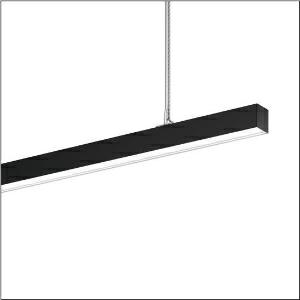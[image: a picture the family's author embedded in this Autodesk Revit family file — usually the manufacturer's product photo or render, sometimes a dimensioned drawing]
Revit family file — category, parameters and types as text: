
# Revit family: silica_r__21_51mx30da44bb_2b52
name_source: partatom
category: Lighting Fixtures
units: mm (PartAtom-declared; Revit-internal decimal feet)

## family parameters
Cut with Voids When Loaded = No
Host = Face
Light Source = No
Part Type = Normal
Room Calculation Point = No
Round Connector Dimension = Use Diameter
Shared = No

## types (1)
- --- (1 x LED, 4210 lm, 26 W, 4000K)
    Apparent Load = 26 VA
    CIE Flux Codes = 47 79 96 57 100
    Color Rendering = 80
    Color Temperature = 4000K
    Default Elevation = 1800 mm
    Description = Silica® 21, office luminaire, primary optical cover: cover, of PMMA, opal, light emission: direct/indirect distribution, primary light characteristic: symmetric, installation type: suspended mounting, LED, rated luminous flux: 4.210lm, luminous efficacy: 162lm/W, light colour: 840, colour temperature: 4000K, with terminal, 3+2-pole, max. 2.5mm², mains connection: 220..240V, AC, 50/60Hz, rated input power: 26W, luminaire housing, of aluminium, jet black (RAL 9005), length: 1.204mm, width: 53mm, height: 53mm, protection rating (complete): IP20, insulation class (complete): insulation class I (protective earthing), certification: CE, permissible operating ambient temperature: 0..+35°C, standard: EN 50419, packaging unit: 1 piece
    Height = 53 mm
    Lamp = 1 x LED
    Lamp Light Flux = 4210 lm
    Lamp Power = 26 W
    Lamp count = 1
    Length = 1204 mm
    Luminous efficacy = 162 lm/W
    Manufacturer = Siteco
    ModVariant = No
    Model = 51MX30DA44BB
    Mounting Place = Ceiling
    Mounting Type = Pendant
    Number of Poles = 1
    OnlyDefault = Yes
    Power Factor = 1
    Product Name = Silica® 21
    Product group = office luminaire | ceiling pendant
    ProductGroupID = 902
    Protection Class = Protection class I
    Protection Degree = IP 20
    RLX_Detail_Level = 1
    RLX_Emergency_Light_Flux = 0 lm
    RLX_Emergency_Type = 0
    RLX_Emergency_Type_DB = No
    RlxData = <blob elided: 25777 chars, md5=d335745c>
    Socket = socket
    Standby Power = 0 W
    System Light Flux = 4210 lm
    System Power = 26 W
    Type Comments = factory setting: luminous flux: 100 % | dim-lin: 254 | 218 mA
    Type Image = l_1297744.jpg
    URL = http://relux.com
    VarID = @adj_047389
    Voltage = 0 V
    Weight = 0.00 kg
    Width = 53 mm

## geometry (parser evidence)
native form markers: Blend x4, Sweep x14
no freeform markers — native parametric forms only
